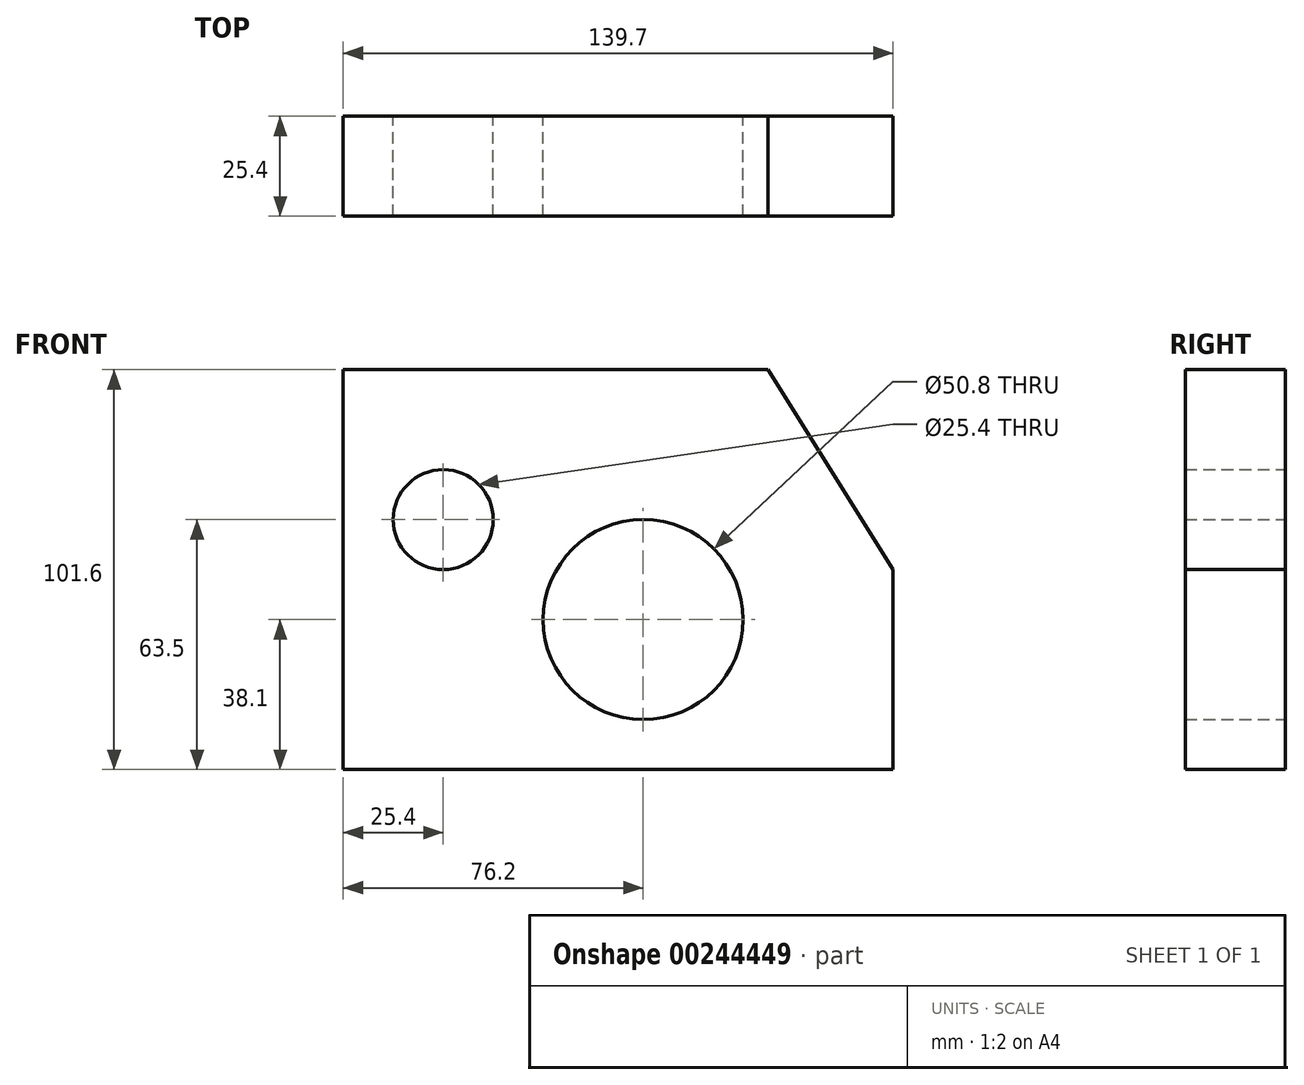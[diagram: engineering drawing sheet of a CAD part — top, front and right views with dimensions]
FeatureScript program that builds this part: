
annotation { "Feature Type Name" : "Feature", "Feature Type Description" : "" }
export const myFeature = defineFeature(function(context is Context, id is Id, definition is map)
    precondition{}
    {
        {
            var Q0;
            Q0=qCreatedBy(makeId("Front.planeOp"),FACE);
            var sketch = newSketch(context, id + "F0", { "sketchPlane" : qUnion([Q0])});
            skLineSegment(sketch, "E0", {"start": v(63.5, -38.1) * mm, "end": v(-76.2, -38.1) * mm});
            skLineSegment(sketch, "E1", {"start": v(-76.2, -38.1) * mm, "end": v(-76.2, 63.5) * mm});
            skLineSegment(sketch, "E2", {"start": v(-76.2, 63.5) * mm, "end": v(31.75, 63.5) * mm});
            skLineSegment(sketch, "E3", {"start": v(31.75, 63.5) * mm, "end": v(63.5, 12.7) * mm});
            skLineSegment(sketch, "E4", {"start": v(63.5, 12.7) * mm, "end": v(63.5, -38.1) * mm});
            skCircle(sketch, "E5", {"center": v(0, 0) * mm, "radius": 25.4 * mm});
            skCircle(sketch, "E6", {"center": v(0, 0) * mm, "radius": 12.7 * mm});
            skCircle(sketch, "E7", {"center": v(-50.8, 25.4) * mm, "radius": 12.7 * mm});
            skSolve(sketch);
        }
        {
            var Q0;
            Q0=makeQuery(id+"F0.imprint","IMPRINT",FACE,{"disambiguationData":[TD([[makeQuery(id+"F0.imprint","IMPRINT",EDGE,{"derivedFrom":sQuery(id+"F0.wireOp",EDGE,"E0")}),-1.0]])]});
            extrude(context, id + "F1", {"entities" : qUnion([Q0]), "depth" : 25.4 * mm});
        }
    });
